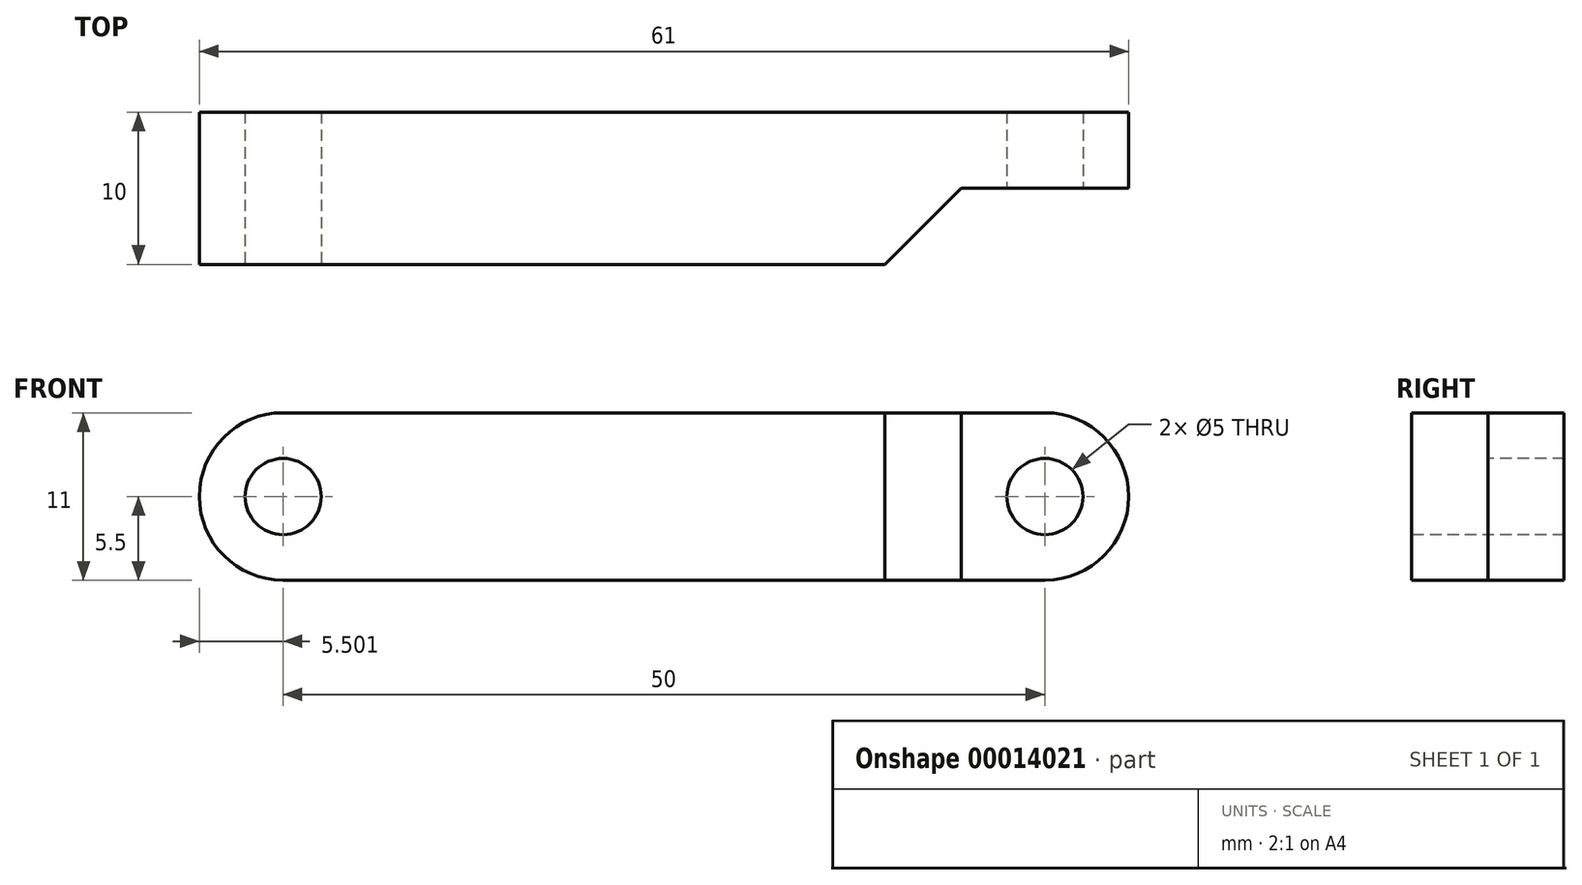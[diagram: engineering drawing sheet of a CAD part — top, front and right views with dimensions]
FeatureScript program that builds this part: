
annotation { "Feature Type Name" : "Feature", "Feature Type Description" : "" }
export const myFeature = defineFeature(function(context is Context, id is Id, definition is map)
    precondition{}
    {
        {
            var Q0;
            Q0=qCreatedBy(makeId("Top.planeOp"),FACE);
            var sketch = newSketch(context, id + "F0", { "sketchPlane" : qUnion([Q0])});
            skLineSegment(sketch, "E0", {"start": v(-26.47, -25) * mm, "end": v(-26.47, 25) * mm, "construction": true});
            skLineSegment(sketch, "E1", {"start": v(-31.97, 25) * mm, "end": v(-20.97, 25) * mm, "construction": true});
            skLineSegment(sketch, "E2", {"start": v(-20.97, 25) * mm, "end": v(-20.97, -25) * mm});
            skLineSegment(sketch, "E3", {"start": v(-20.97, -25) * mm, "end": v(-31.97, -25) * mm, "construction": true});
            skLineSegment(sketch, "E4", {"start": v(-31.97, -25) * mm, "end": v(-31.97, 25) * mm});
            skArc(sketch, "E5", {"start": v(-20.97, 25) * mm, "mid": v(-26.47, 30.5) * mm, "end": v(-31.97, 25) * mm});
            skArc(sketch, "E6", {"start": v(-31.97, -25) * mm, "mid": v(-26.47, -30.5) * mm, "end": v(-20.97, -25) * mm});
            skCircle(sketch, "E7", {"center": v(-26.47, 25) * mm, "radius": 2.5 * mm});
            skCircle(sketch, "E8", {"center": v(-26.47, -25) * mm, "radius": 2.5 * mm});
            skPoint(sketch, "E9", {"position": v(-26.47, 0) * mm});
            skLineSegment(sketch, "E10", {"start": v(20.72, 70) * mm, "end": v(20.72, -70) * mm, "construction": true});
            skPoint(sketch, "E11", {"position": v(20.72, 0) * mm});
            skCircle(sketch, "E12", {"center": v(20.72, 70) * mm, "radius": 2.5 * mm});
            skCircle(sketch, "E13", {"center": v(20.72, -70) * mm, "radius": 2.5 * mm});
            skLineSegment(sketch, "E14.bottom", {"start": v(15.22, 70) * mm, "end": v(26.22, 70) * mm, "construction": true});
            skLineSegment(sketch, "E14.top", {"start": v(15.22, -70) * mm, "end": v(26.22, -70) * mm, "construction": true});
            skLineSegment(sketch, "E14.left", {"start": v(15.22, 70) * mm, "end": v(15.22, -70) * mm});
            skLineSegment(sketch, "E14.right", {"start": v(26.22, 70) * mm, "end": v(26.22, -70) * mm});
            skArc(sketch, "E15", {"start": v(26.22, 70) * mm, "mid": v(20.72, 75.5) * mm, "end": v(15.22, 70) * mm});
            skArc(sketch, "E16", {"start": v(15.22, -70) * mm, "mid": v(20.72, -75.5) * mm, "end": v(26.22, -70) * mm});
            skSolve(sketch);
        }
        {
            var Q0;
            Q0=makeQuery(id+"F0.imprint","IMPRINT",FACE,{"disambiguationData":[TD([[makeQuery(id+"F0.imprint","IMPRINT",EDGE,{"derivedFrom":sQuery(id+"F0.wireOp",EDGE,"E2")}),-1.0]])]});
            extrude(context, id + "F1", {"entities" : qUnion([Q0]), "depth" : 10 * mm});
        }
        {
            var Q0;
            Q0=makeQuery(id+"F1.opExtrude","SWEPT_FACE",FACE,{"disambiguationData":[OSD([sQuery(id+"F0.wireOp",EDGE,"E4")])]});
            var sketch = newSketch(context, id + "F2", { "sketchPlane" : qUnion([Q0])});
            skLineSegment(sketch, "E17.0.0", {"start": v(-25, 0) * mm, "end": v(25, 0) * mm, "construction": true});
            skLineSegment(sketch, "E17.0.1", {"start": v(25, 0) * mm, "end": v(25, 10) * mm, "construction": true});
            skLineSegment(sketch, "E17.0.2", {"start": v(25, 10) * mm, "end": v(-25, 10) * mm, "construction": true});
            skLineSegment(sketch, "E17.0.3", {"start": v(-25, 10) * mm, "end": v(-25, 0) * mm, "construction": true});
            skLineSegment(sketch, "E18", {"start": v(-30.5, 0) * mm, "end": v(-30.5, 10) * mm, "construction": true});
            skLineSegment(sketch, "E19", {"start": v(30.5, 10) * mm, "end": v(30.5, 0) * mm, "construction": true});
            skLineSegment(sketch, "E20", {"start": v(-30.5, 10) * mm, "end": v(-25, 10) * mm, "construction": true});
            skLineSegment(sketch, "E21", {"start": v(-30.5, 0) * mm, "end": v(-25, 0) * mm, "construction": true});
            skLineSegment(sketch, "E22", {"start": v(25, 10) * mm, "end": v(30.5, 10) * mm, "construction": true});
            skLineSegment(sketch, "E23", {"start": v(30.5, 0) * mm, "end": v(25, 0) * mm, "construction": true});
            skLineSegment(sketch, "E24", {"start": v(30.5, 5) * mm, "end": v(-30.5, 5) * mm, "construction": true});
            skLineSegment(sketch, "E25", {"start": v(0, 10) * mm, "end": v(0, 0) * mm, "construction": true});
            skCircle(sketch, "E26", {"center": v(0, 5) * mm, "radius": 5 * mm, "construction": true});
            skLineSegment(sketch, "E27", {"start": v(0, 10) * mm, "end": v(-5, 5) * mm});
            skLineSegment(sketch, "E28", {"start": v(-5, 5) * mm, "end": v(-30.5, 5) * mm});
            skLineSegment(sketch, "E29", {"start": v(-30.5, 0) * mm, "end": v(-30.5, 5) * mm});
            skLineSegment(sketch, "E30", {"start": v(-30.5, 0) * mm, "end": v(0, 0) * mm});
            skLineSegment(sketch, "E31", {"start": v(0, 0) * mm, "end": v(5, 5) * mm});
            skLineSegment(sketch, "E32", {"start": v(5, 5) * mm, "end": v(30.5, 5) * mm});
            skLineSegment(sketch, "E33", {"start": v(30.5, 5) * mm, "end": v(30.5, 10) * mm});
            skLineSegment(sketch, "E34", {"start": v(30.5, 10) * mm, "end": v(0, 10) * mm});
            skSolve(sketch);
        }
        {
            var Q0;
            {var subQ5=sQuery(id+"F2.wireOp",EDGE,"E29");Q0=makeQuery(id+"F2.imprint","IMPRINT",FACE,{"disambiguationData":[TD([[makeQuery(id+"F2.imprint","IMPRINT",EDGE,{"derivedFrom":subQ5}),-1.0]])]});}
            var Q1;
            {var subQ11=sQuery(id+"F2.wireOp",EDGE,"E27");Q1=makeQuery(id+"F2.imprint","IMPRINT",FACE,{"disambiguationData":[TD([[makeQuery(id+"F2.imprint","IMPRINT",EDGE,{"derivedFrom":subQ11}),1.0]])]});}
            var Q2;
            {var subQ5=sQuery(id+"F2.wireOp",EDGE,"E33");Q2=makeQuery(id+"F2.imprint","IMPRINT",FACE,{"disambiguationData":[TD([[makeQuery(id+"F2.imprint","IMPRINT",EDGE,{"derivedFrom":subQ5}),1.0]])]});}
            var Q3;
            Q3=makeQuery(id+"F1.opExtrude","SWEPT_FACE",FACE,{"disambiguationData":[OSD([sQuery(id+"F0.wireOp",EDGE,"E2")])]});
            extrude(context, id + "F3", {"entities" : qUnion([Q0, Q1, Q2]), "operationType" : NewBodyOperationType.INTERSECT, "endBound" : BoundingType.UP_TO_SURFACE, "oppositeDirection" : true, "endBoundEntityFace" : qUnion([Q3]), "depth" : 25 * mm});
        }
        {
            var Q0;
            Q0=makeQuery(id+"F0.imprint","IMPRINT",FACE,{"disambiguationData":[TD([[makeQuery(id+"F0.imprint","IMPRINT",EDGE,{"derivedFrom":sQuery(id+"F0.wireOp",EDGE,"E2")}),-1.0]])]});
            extrude(context, id + "F4", {"entities" : qUnion([Q0]), "depth" : 70 * mm, "hasSecondDirection" : true, "secondDirectionOppositeDirection" : false, "secondDirectionDepth" : 50 * mm});
        }
        {
            var Q0;
            Q0=makeQuery(id+"F4.opExtrude","SWEPT_FACE",FACE,{"disambiguationData":[OSD([sQuery(id+"F0.wireOp",EDGE,"E4")])]});
            var sketch = newSketch(context, id + "F5", { "sketchPlane" : qUnion([Q0])});
            skPoint(sketch, "E35.0", {"position": v(-25, 70) * mm});
            skLineSegment(sketch, "E36", {"start": v(-30.5, 50) * mm, "end": v(-30.5, 70) * mm, "construction": true});
            skPoint(sketch, "E37.0", {"position": v(-25, 50) * mm});
            skLineSegment(sketch, "E38", {"start": v(30.5, 70) * mm, "end": v(30.5, 50) * mm, "construction": true});
            skLineSegment(sketch, "E39", {"start": v(-30.5, 60) * mm, "end": v(-19.5, 60) * mm, "construction": true});
            skLineSegment(sketch, "E40", {"start": v(-30.5, 70) * mm, "end": v(-17.43, 70) * mm});
            skLineSegment(sketch, "E41", {"start": v(-17.43, 70) * mm, "end": v(-12.43, 65) * mm});
            skLineSegment(sketch, "E42", {"start": v(-12.43, 65) * mm, "end": v(30.5, 65) * mm});
            skLineSegment(sketch, "E43", {"start": v(30.5, 65) * mm, "end": v(30.5, 55) * mm});
            skLineSegment(sketch, "E44", {"start": v(30.5, 55) * mm, "end": v(-12.43, 55) * mm});
            skLineSegment(sketch, "E45", {"start": v(-12.43, 55) * mm, "end": v(-17.43, 50) * mm});
            skLineSegment(sketch, "E46", {"start": v(-17.43, 50) * mm, "end": v(-30.5, 50) * mm});
            skLineSegment(sketch, "E47", {"start": v(-30.5, 70) * mm, "end": v(-30.5, 65) * mm});
            skLineSegment(sketch, "E48", {"start": v(-30.5, 65) * mm, "end": v(-19.5, 65) * mm});
            skLineSegment(sketch, "E49", {"start": v(-19.5, 65) * mm, "end": v(-19.5, 55) * mm});
            skLineSegment(sketch, "E50", {"start": v(-19.5, 55) * mm, "end": v(-30.5, 55) * mm});
            skLineSegment(sketch, "E51", {"start": v(-30.5, 55) * mm, "end": v(-30.5, 50) * mm});
            skCircle(sketch, "E52", {"center": v(-19.5, 65) * mm, "radius": 5 * mm, "construction": true});
            skLineSegment(sketch, "E53", {"start": v(30.5, 60) * mm, "end": v(19.5, 60) * mm});
            skLineSegment(sketch, "E54", {"start": v(19.5, 60) * mm, "end": v(19.5, 55) * mm});
            skSolve(sketch);
        }
        {
            var Q0;
            {var subQ19=sQuery(id+"F5.wireOp",EDGE,"E41");Q0=makeQuery(id+"F5.imprint","IMPRINT",FACE,{"disambiguationData":[TD([[makeQuery(id+"F5.imprint","IMPRINT",EDGE,{"derivedFrom":subQ19}),-1.0]])]});}
            var Q1;
            {var subQ5=sQuery(id+"F5.wireOp",EDGE,"E51");Q1=makeQuery(id+"F5.imprint","IMPRINT",FACE,{"disambiguationData":[TD([[makeQuery(id+"F5.imprint","IMPRINT",EDGE,{"derivedFrom":subQ5}),1.0]])]});}
            var Q2;
            {var subQ3=sQuery(id+"F5.wireOp",EDGE,"E42");var subQ5=sQuery(id+"F5.wireOp",EDGE,"E43");var subQ7=makeQuery(id+"F5.imprint","INTERSECT",VERTEX,{"derivedFrom":[subQ3,subQ5]});Q2=makeQuery(id+"F5.imprint","IMPRINT",FACE,{"disambiguationData":[TD([[makeQuery(id+"F5.imprint","IMPRINT",EDGE,{"disambiguationData":[TD([[subQ7,-1.0]])],"derivedFrom":subQ5}),-1.0]])]});}
            var Q3;
            {var subQ5=sQuery(id+"F5.wireOp",EDGE,"E47");Q3=makeQuery(id+"F5.imprint","IMPRINT",FACE,{"disambiguationData":[TD([[makeQuery(id+"F5.imprint","IMPRINT",EDGE,{"derivedFrom":subQ5}),1.0]])]});}
            var Q4;
            Q4=makeQuery(id+"F4.opExtrude","SWEPT_FACE",FACE,{"disambiguationData":[OSD([sQuery(id+"F0.wireOp",EDGE,"E2")])]});
            extrude(context, id + "F6", {"entities" : qUnion([Q0, Q1, Q2, Q3]), "operationType" : NewBodyOperationType.INTERSECT, "endBound" : BoundingType.UP_TO_SURFACE, "oppositeDirection" : true, "endBoundEntityFace" : qUnion([Q4]), "depth" : 25 * mm});
        }
        {
            var Q0;
            Q0=makeQuery(id+"F0.imprint","IMPRINT",FACE,{"disambiguationData":[TD([[makeQuery(id+"F0.imprint","IMPRINT",EDGE,{"derivedFrom":sQuery(id+"F0.wireOp",EDGE,"E12")}),-1.0]])]});
            extrude(context, id + "F7", {"entities" : qUnion([Q0]), "depth" : 20 * mm});
        }
        {
            var Q0;
            Q0=makeQuery(id+"F7.opExtrude","SWEPT_FACE",FACE,{"disambiguationData":[OSD([sQuery(id+"F0.wireOp",EDGE,"E14.left")])]});
            var sketch = newSketch(context, id + "F8", { "sketchPlane" : qUnion([Q0])});
            skLineSegment(sketch, "E55", {"start": v(-75.5, 0) * mm, "end": v(-75.5, 20) * mm, "construction": true});
            skPoint(sketch, "E56.0", {"position": v(-70, 20) * mm});
            skPoint(sketch, "E57.0", {"position": v(-70, 0) * mm});
            skLineSegment(sketch, "E58", {"start": v(75.5, 20) * mm, "end": v(75.5, 0) * mm, "construction": true});
            skLineSegment(sketch, "E59", {"start": v(-75.5, 10) * mm, "end": v(75.5, 10) * mm, "construction": true});
            skLineSegment(sketch, "E60", {"start": v(-75.5, 20) * mm, "end": v(75.5, 20) * mm, "construction": true});
            skLineSegment(sketch, "E61", {"start": v(75.5, 0) * mm, "end": v(-75.5, 0) * mm, "construction": true});
            skLineSegment(sketch, "E62", {"start": v(-75.5, 10) * mm, "end": v(-35.5, 10) * mm, "construction": true});
            skLineSegment(sketch, "E63", {"start": v(-75.5, 20) * mm, "end": v(-33.43, 20) * mm});
            skLineSegment(sketch, "E64", {"start": v(-33.43, 20) * mm, "end": v(-18.43, 5) * mm});
            skLineSegment(sketch, "E65", {"start": v(-18.43, 5) * mm, "end": v(75.5, 5) * mm});
            skLineSegment(sketch, "E66", {"start": v(75.5, 5) * mm, "end": v(75.5, 0) * mm});
            skLineSegment(sketch, "E67", {"start": v(75.5, 0) * mm, "end": v(-75.5, 0) * mm});
            skLineSegment(sketch, "E68", {"start": v(-75.5, 5) * mm, "end": v(-75.5, 0) * mm});
            skLineSegment(sketch, "E69", {"start": v(-75.5, 5) * mm, "end": v(-35.5, 5) * mm});
            skLineSegment(sketch, "E70", {"start": v(-35.5, 5) * mm, "end": v(-35.5, 15) * mm});
            skLineSegment(sketch, "E71", {"start": v(-35.5, 15) * mm, "end": v(-75.5, 15) * mm});
            skLineSegment(sketch, "E72", {"start": v(-75.5, 15) * mm, "end": v(-75.5, 20) * mm});
            skLineSegment(sketch, "E73", {"start": v(-18.43, 10) * mm, "end": v(-18.43, 0) * mm, "construction": true});
            skCircle(sketch, "E74", {"center": v(-35.5, 15) * mm, "radius": 5 * mm, "construction": true});
            skSolve(sketch);
        }
        {
            var Q0;
            {var subQ0=sQuery(id+"F8.wireOp",EDGE,"E72");Q0=makeQuery(id+"F8.imprint","IMPRINT",FACE,{"disambiguationData":[TD([[makeQuery(id+"F8.imprint","IMPRINT",EDGE,{"derivedFrom":subQ0}),-1.0]])]});}
            var Q1;
            {var subQ15=sQuery(id+"F8.wireOp",EDGE,"E64");Q1=makeQuery(id+"F8.imprint","IMPRINT",FACE,{"disambiguationData":[TD([[makeQuery(id+"F8.imprint","IMPRINT",EDGE,{"derivedFrom":subQ15}),-1.0]])]});}
            var Q2;
            {var subQ5=sQuery(id+"F8.wireOp",EDGE,"E68");Q2=makeQuery(id+"F8.imprint","IMPRINT",FACE,{"disambiguationData":[TD([[makeQuery(id+"F8.imprint","IMPRINT",EDGE,{"derivedFrom":subQ5}),1.0]])]});}
            var Q3;
            {var subQ5=sQuery(id+"F8.wireOp",EDGE,"E66");Q3=makeQuery(id+"F8.imprint","IMPRINT",FACE,{"disambiguationData":[TD([[makeQuery(id+"F8.imprint","IMPRINT",EDGE,{"derivedFrom":subQ5}),-1.0]])]});}
            var Q4;
            Q4=makeQuery(id+"F7.opExtrude","SWEPT_FACE",FACE,{"disambiguationData":[OSD([sQuery(id+"F0.wireOp",EDGE,"E14.right")])]});
            extrude(context, id + "F9", {"entities" : qUnion([Q0, Q1, Q2, Q3]), "operationType" : NewBodyOperationType.INTERSECT, "endBound" : BoundingType.UP_TO_SURFACE, "oppositeDirection" : true, "endBoundEntityFace" : qUnion([Q4]), "depth" : 25 * mm});
        }
        {
            var Q0;
            Q0=makeQuery(id+"F0.imprint","IMPRINT",FACE,{"disambiguationData":[TD([[makeQuery(id+"F0.imprint","IMPRINT",EDGE,{"derivedFrom":sQuery(id+"F0.wireOp",EDGE,"E13")}),1.0]])]});
            extrude(context, id + "F10", {"entities" : qUnion([Q0]), "depth" : 30 * mm, "hasSecondDirection" : true, "secondDirectionOppositeDirection" : false, "secondDirectionDepth" : 20 * mm});
        }
        {
            var Q0;
            Q0=makeQuery(id+"F0.imprint","IMPRINT",FACE,{"disambiguationData":[TD([[makeQuery(id+"F0.imprint","IMPRINT",EDGE,{"derivedFrom":sQuery(id+"F0.wireOp",EDGE,"E13")}),1.0]])]});
            extrude(context, id + "F11", {"entities" : qUnion([Q0]), "depth" : 70 * mm, "hasSecondDirection" : true, "secondDirectionOppositeDirection" : false, "secondDirectionDepth" : 50 * mm});
        }
        {
            var Q0;
            Q0=makeQuery(id+"F0.imprint","IMPRINT",FACE,{"disambiguationData":[TD([[makeQuery(id+"F0.imprint","IMPRINT",EDGE,{"derivedFrom":sQuery(id+"F0.wireOp",EDGE,"E2")}),-1.0]])]});
            extrude(context, id + "F12", {"entities" : qUnion([Q0]), "oppositeDirection" : true, "depth" : 30 * mm, "hasSecondDirection" : true, "secondDirectionOppositeDirection" : true, "secondDirectionDepth" : 20 * mm});
        }
        {
            var Q0;
            Q0=makeQuery(id+"F12.opExtrude","SWEPT_FACE",FACE,{"disambiguationData":[OSD([sQuery(id+"F0.wireOp",EDGE,"E4")])]});
            var sketch = newSketch(context, id + "F13", { "sketchPlane" : qUnion([Q0])});
            skLineSegment(sketch, "E75", {"start": v(-30.5, -30) * mm, "end": v(-30.5, -20) * mm, "construction": true});
            skPoint(sketch, "E76.0", {"position": v(-25, -20) * mm});
            skPoint(sketch, "E77.0", {"position": v(-25, -30) * mm});
            skLineSegment(sketch, "E78", {"start": v(30.5, -20) * mm, "end": v(30.5, -30) * mm});
            skLineSegment(sketch, "E79", {"start": v(30.5, -20) * mm, "end": v(-14.5, -20) * mm});
            skLineSegment(sketch, "E80", {"start": v(-14.5, -20) * mm, "end": v(-30.5, -20) * mm, "construction": true});
            skLineSegment(sketch, "E81", {"start": v(-30.5, -30) * mm, "end": v(30.5, -30) * mm});
            skLineSegment(sketch, "E82", {"start": v(-30.5, -25) * mm, "end": v(-19.5, -25) * mm});
            skLineSegment(sketch, "E83", {"start": v(-19.5, -25) * mm, "end": v(-14.5, -20) * mm});
            skLineSegment(sketch, "E84", {"start": v(-30.5, -25) * mm, "end": v(-30.5, -30) * mm});
            skSolve(sketch);
        }
        {
            var Q0;
            {var subQ0=sQuery(id+"F13.wireOp",EDGE,"E84");Q0=makeQuery(id+"F13.imprint","IMPRINT",FACE,{"disambiguationData":[TD([[makeQuery(id+"F13.imprint","IMPRINT",EDGE,{"derivedFrom":subQ0}),1.0]])]});}
            var Q1;
            {var subQ7=sQuery(id+"F13.wireOp",EDGE,"E83");Q1=makeQuery(id+"F13.imprint","IMPRINT",FACE,{"disambiguationData":[TD([[makeQuery(id+"F13.imprint","IMPRINT",EDGE,{"derivedFrom":subQ7}),-1.0]])]});}
            var Q2;
            {var subQ2=sQuery(id+"F13.wireOp",EDGE,"E78");Q2=makeQuery(id+"F13.imprint","IMPRINT",FACE,{"disambiguationData":[TD([[makeQuery(id+"F13.imprint","IMPRINT",EDGE,{"derivedFrom":subQ2}),-1.0]])]});}
            var Q3;
            Q3=makeQuery(id+"F12.opExtrude","SWEPT_FACE",FACE,{"disambiguationData":[OSD([sQuery(id+"F0.wireOp",EDGE,"E2")])]});
            extrude(context, id + "F14", {"entities" : qUnion([Q0, Q1, Q2]), "operationType" : NewBodyOperationType.INTERSECT, "endBound" : BoundingType.UP_TO_SURFACE, "oppositeDirection" : true, "endBoundEntityFace" : qUnion([Q3]), "depth" : 25 * mm});
        }
        {
            var Q0;
            Q0=makeQuery(id+"F12.opExtrude","SWEPT_BODY",BODY,{"disambiguationData":[OSD([sQuery(id+"F0.wireOp",EDGE,"E2"),sQuery(id+"F0.wireOp",EDGE,"E4"),sQuery(id+"F0.wireOp",EDGE,"E5"),sQuery(id+"F0.wireOp",EDGE,"E6"),sQuery(id+"F0.wireOp",EDGE,"E7"),sQuery(id+"F0.wireOp",EDGE,"E8")])]});
            var Q1;
            Q1=makeQuery(id+"F12.opExtrude","SWEPT_EDGE",EDGE,{"disambiguationData":[OSD([sQuery(id+"F0.wireOp",EDGE,"E4"),sQuery(id+"F0.wireOp",EDGE,"E6")])]});
            transform(context, id + "F15", {"entities" : qUnion([Q0]), "transformType" : TransformType.ROTATION, "transformAxis" : qUnion([Q1]), "angle" : 90 * degree, "oppositeDirection" : true, "makeCopy" : false});
        }
        {
            var Q0;
            Q0=makeQuery(id+"F12.opExtrude","SWEPT_BODY",BODY,{"disambiguationData":[OSD([sQuery(id+"F0.wireOp",EDGE,"E2"),sQuery(id+"F0.wireOp",EDGE,"E4"),sQuery(id+"F0.wireOp",EDGE,"E5"),sQuery(id+"F0.wireOp",EDGE,"E6"),sQuery(id+"F0.wireOp",EDGE,"E7"),sQuery(id+"F0.wireOp",EDGE,"E8")])]});
            var Q1;
            Q1=makeQuery(id+"F12.opExtrude","CAP_EDGE",EDGE,{"disambiguationData":[OSD([sQuery(id+"F0.wireOp",EDGE,"E2")])],"isStart":true});
            transform(context, id + "F16", {"entities" : qUnion([Q0]), "transformType" : TransformType.ROTATION, "transformAxis" : qUnion([Q1]), "angle" : 90 * degree, "oppositeDirection" : true, "makeCopy" : false});
        }
    });
